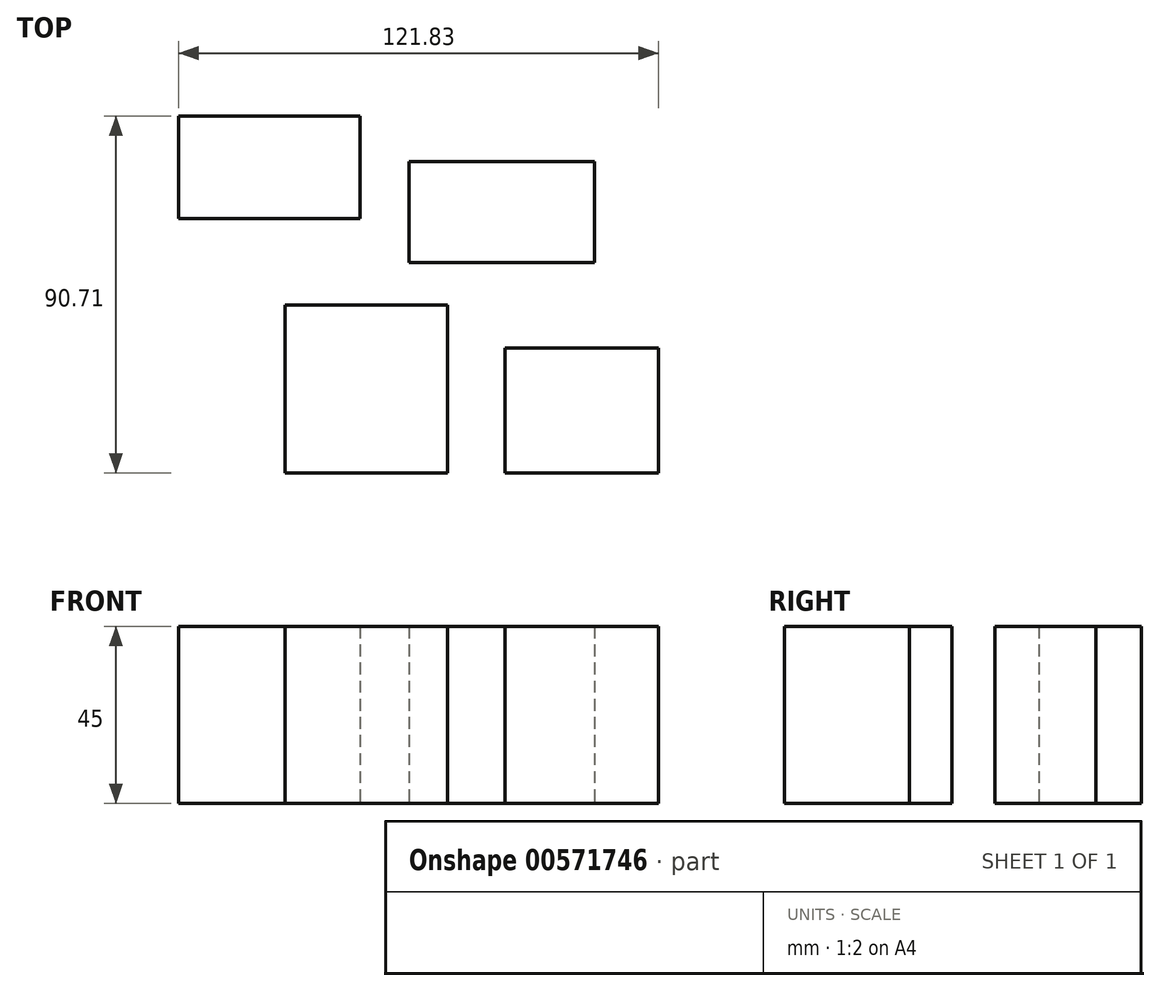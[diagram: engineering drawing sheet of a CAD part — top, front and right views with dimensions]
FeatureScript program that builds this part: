
annotation { "Feature Type Name" : "Feature", "Feature Type Description" : "" }
export const myFeature = defineFeature(function(context is Context, id is Id, definition is map)
    precondition{}
    {
        {
            var Q0;
            Q0=qCreatedBy(makeId("Top.planeOp"),FACE);
            var sketch = newSketch(context, id + "F0", { "sketchPlane" : qUnion([Q0])});
            skLineSegment(sketch, "E0.bottom", {"start": v(-31.44, 0) * mm, "end": v(9.79, 0) * mm});
            skLineSegment(sketch, "E0.top", {"start": v(-31.44, -42.61) * mm, "end": v(9.79, -42.61) * mm});
            skLineSegment(sketch, "E0.left", {"start": v(-31.44, 0) * mm, "end": v(-31.44, -42.61) * mm});
            skLineSegment(sketch, "E0.right", {"start": v(9.79, 0) * mm, "end": v(9.79, -42.61) * mm});
            skLineSegment(sketch, "E1.bottom", {"start": v(0, 36.54) * mm, "end": v(47.06, 36.54) * mm});
            skLineSegment(sketch, "E1.top", {"start": v(0, 10.91) * mm, "end": v(47.06, 10.91) * mm});
            skLineSegment(sketch, "E1.left", {"start": v(0, 36.54) * mm, "end": v(0, 10.91) * mm});
            skLineSegment(sketch, "E1.right", {"start": v(47.06, 36.54) * mm, "end": v(47.06, 10.91) * mm});
            skLineSegment(sketch, "E2.bottom", {"start": v(24.44, -10.8) * mm, "end": v(63.35, -10.8) * mm});
            skLineSegment(sketch, "E2.top", {"start": v(24.44, -42.61) * mm, "end": v(63.35, -42.61) * mm});
            skLineSegment(sketch, "E2.left", {"start": v(24.44, -10.8) * mm, "end": v(24.44, -42.61) * mm});
            skLineSegment(sketch, "E2.right", {"start": v(63.35, -10.8) * mm, "end": v(63.35, -42.61) * mm});
            skLineSegment(sketch, "E3.bottom", {"start": v(-58.48, 48.1) * mm, "end": v(-12.42, 48.1) * mm});
            skLineSegment(sketch, "E3.top", {"start": v(-58.48, 22.07) * mm, "end": v(-12.42, 22.07) * mm});
            skLineSegment(sketch, "E3.left", {"start": v(-58.48, 48.1) * mm, "end": v(-58.48, 22.07) * mm});
            skLineSegment(sketch, "E3.right", {"start": v(-12.42, 48.1) * mm, "end": v(-12.42, 22.07) * mm});
            skSolve(sketch);
        }
        {
            var Q0;
            Q0 = qSketchRegion(id + "F0", true);
            extrude(context, id + "F1", {"entities" : qUnion([Q0]), "depth" : 45 * mm, "offsetDistance" : 25 * mm});
        }
    });
